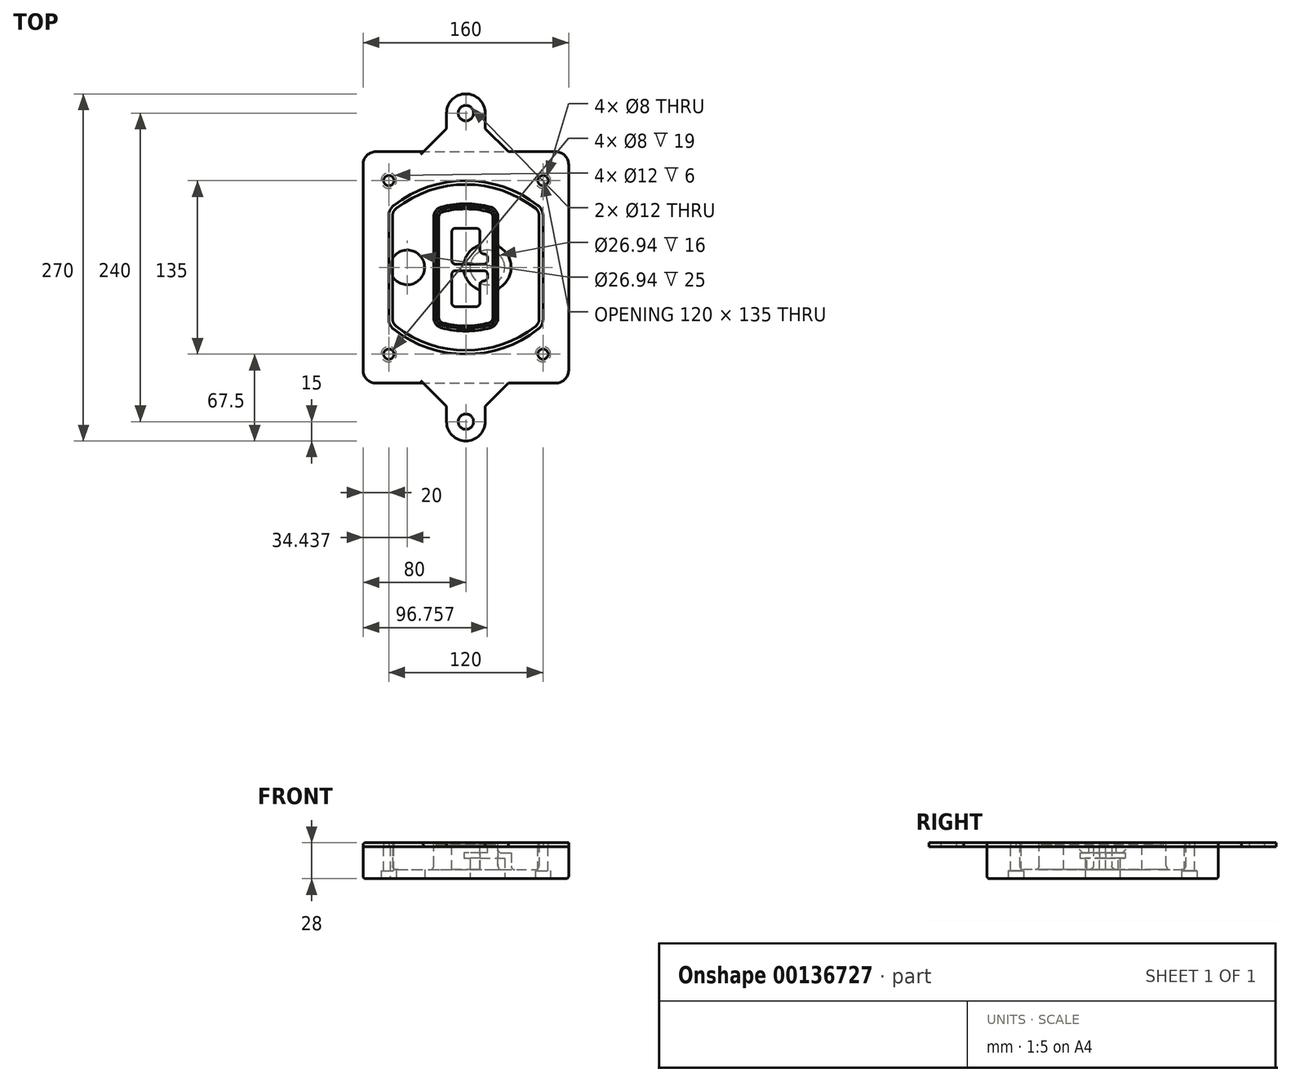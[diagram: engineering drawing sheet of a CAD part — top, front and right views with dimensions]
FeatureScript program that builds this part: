
annotation { "Feature Type Name" : "Feature", "Feature Type Description" : "" }
export const myFeature = defineFeature(function(context is Context, id is Id, definition is map)
    precondition{}
    {
        {
            var Q0;
            Q0=qCreatedBy(makeId("Top.planeOp"),FACE);
            var sketch = newSketch(context, id + "F0", { "sketchPlane" : qUnion([Q0])});
            skPoint(sketch, "E0.rect.middle", {"position": v(0, 0) * mm});
            skLineSegment(sketch, "E1.bottom", {"start": v(-70, -90) * mm, "end": v(70, -90) * mm});
            skLineSegment(sketch, "E1.top", {"start": v(-70, 90) * mm, "end": v(70, 90) * mm});
            skLineSegment(sketch, "E1.left", {"start": v(-80, -80) * mm, "end": v(-80, 80) * mm});
            skLineSegment(sketch, "E1.right", {"start": v(80, -80) * mm, "end": v(80, 80) * mm});
            skLineSegment(sketch, "E2", {"start": v(-80, 90) * mm, "end": v(80, -90) * mm, "construction": true});
            skLineSegment(sketch, "E3", {"start": v(80, 90) * mm, "end": v(-80, -90) * mm, "construction": true});
            skCircle(sketch, "E4", {"center": v(-60, 67.5) * mm, "radius": 4 * mm});
            skCircle(sketch, "E5", {"center": v(60, 67.5) * mm, "radius": 4 * mm});
            skCircle(sketch, "E6", {"center": v(60, -67.5) * mm, "radius": 4 * mm});
            skCircle(sketch, "E7", {"center": v(-60, -67.5) * mm, "radius": 4 * mm});
            skLineSegment(sketch, "E8", {"start": v(-60, 67.5) * mm, "end": v(60, 67.5) * mm, "construction": true});
            skLineSegment(sketch, "E9", {"start": v(60, 67.5) * mm, "end": v(60, -67.5) * mm, "construction": true});
            skLineSegment(sketch, "E10", {"start": v(60, -67.5) * mm, "end": v(-60, -67.5) * mm, "construction": true});
            skLineSegment(sketch, "E11", {"start": v(-60, -67.5) * mm, "end": v(-60, 67.5) * mm, "construction": true});
            skLineSegment(sketch, "E12", {"start": v(-60, 40.3) * mm, "end": v(-60, -40.3) * mm});
            skLineSegment(sketch, "E13", {"start": v(60, 40.3) * mm, "end": v(60, -40.3) * mm});
            skArc(sketch, "E14", {"start": v(56.15, 48.18) * mm, "mid": v(0, 67.5) * mm, "end": v(-56.15, 48.18) * mm});
            skArc(sketch, "E15", {"start": v(-56.15, -48.18) * mm, "mid": v(0, -67.5) * mm, "end": v(56.15, -48.18) * mm});
            skLineSegment(sketch, "E16", {"start": v(-60, 0) * mm, "end": v(60, 0) * mm, "construction": true});
            skPoint(sketch, "E17.visualSharp", {"position": v(-60, -45) * mm});
            skArc(sketch, "E17.filletArc", {"start": v(-60, -40.3) * mm, "mid": v(-58.99, -44.68) * mm, "end": v(-56.15, -48.18) * mm});
            skPoint(sketch, "E18.visualSharp", {"position": v(-60, 45) * mm});
            skArc(sketch, "E18.filletArc", {"start": v(-56.15, 48.18) * mm, "mid": v(-58.99, 44.68) * mm, "end": v(-60, 40.3) * mm});
            skPoint(sketch, "E19.visualSharp", {"position": v(60, 45) * mm});
            skArc(sketch, "E19.filletArc", {"start": v(60, 40.3) * mm, "mid": v(58.99, 44.68) * mm, "end": v(56.15, 48.18) * mm});
            skPoint(sketch, "E20.visualSharp", {"position": v(60, -45) * mm});
            skArc(sketch, "E20.filletArc", {"start": v(56.15, -48.18) * mm, "mid": v(58.99, -44.68) * mm, "end": v(60, -40.3) * mm});
            skPoint(sketch, "E21.visualSharp", {"position": v(-80, 90) * mm});
            skArc(sketch, "E21.filletArc", {"start": v(-70, 90) * mm, "mid": v(-77.07, 87.07) * mm, "end": v(-80, 80) * mm});
            skPoint(sketch, "E22.visualSharp", {"position": v(80, 90) * mm});
            skArc(sketch, "E22.filletArc", {"start": v(80, 80) * mm, "mid": v(77.07, 87.07) * mm, "end": v(70, 90) * mm});
            skPoint(sketch, "E23.visualSharp", {"position": v(80, -90) * mm});
            skArc(sketch, "E23.filletArc", {"start": v(70, -90) * mm, "mid": v(77.07, -87.07) * mm, "end": v(80, -80) * mm});
            skPoint(sketch, "E24.visualSharp", {"position": v(-80, -90) * mm});
            skArc(sketch, "E24.filletArc", {"start": v(-80, -80) * mm, "mid": v(-77.07, -87.07) * mm, "end": v(-70, -90) * mm});
            skArc(sketch, "E25.0", {"start": v(57, 40.3) * mm, "mid": v(56.3, 43.36) * mm, "end": v(54.3, 45.81) * mm});
            skLineSegment(sketch, "E25.1", {"start": v(57, 40.3) * mm, "end": v(57, -40.3) * mm});
            skArc(sketch, "E25.2", {"start": v(54.3, -45.81) * mm, "mid": v(56.3, -43.36) * mm, "end": v(57, -40.3) * mm});
            skArc(sketch, "E25.3", {"start": v(-54.3, -45.81) * mm, "mid": v(0, -64.5) * mm, "end": v(54.3, -45.81) * mm});
            skArc(sketch, "E25.4", {"start": v(-57, -40.3) * mm, "mid": v(-56.3, -43.36) * mm, "end": v(-54.3, -45.81) * mm});
            skArc(sketch, "E25.5", {"start": v(54.3, 45.81) * mm, "mid": v(0, 64.5) * mm, "end": v(-54.3, 45.81) * mm});
            skLineSegment(sketch, "E25.6", {"start": v(-57, 40.3) * mm, "end": v(-57, -40.3) * mm});
            skArc(sketch, "E25.7", {"start": v(-54.3, 45.81) * mm, "mid": v(-56.3, 43.36) * mm, "end": v(-57, 40.3) * mm});
            skArc(sketch, "E26.0", {"start": v(-58.62, 51.33) * mm, "mid": v(-62.58, 46.43) * mm, "end": v(-64, 40.3) * mm});
            skArc(sketch, "E26.1", {"start": v(58.62, 51.33) * mm, "mid": v(0, 71.5) * mm, "end": v(-58.62, 51.33) * mm});
            skArc(sketch, "E26.2", {"start": v(64, 40.3) * mm, "mid": v(62.58, 46.43) * mm, "end": v(58.62, 51.33) * mm});
            skLineSegment(sketch, "E26.3", {"start": v(64, 40.3) * mm, "end": v(64, -40.3) * mm});
            skArc(sketch, "E26.4", {"start": v(58.62, -51.33) * mm, "mid": v(62.58, -46.43) * mm, "end": v(64, -40.3) * mm});
            skLineSegment(sketch, "E26.5", {"start": v(-64, 40.3) * mm, "end": v(-64, -40.3) * mm});
            skArc(sketch, "E26.6", {"start": v(-58.62, -51.33) * mm, "mid": v(0, -71.5) * mm, "end": v(58.62, -51.33) * mm});
            skArc(sketch, "E26.7", {"start": v(-64, -40.3) * mm, "mid": v(-62.58, -46.43) * mm, "end": v(-58.62, -51.33) * mm});
            skSolve(sketch);
        }
        {
            var Q0;
            Q0=makeQuery(id+"F0.imprint","IMPRINT",FACE,{"disambiguationData":[TD([[makeQuery(id+"F0.imprint","IMPRINT",EDGE,{"derivedFrom":sQuery(id+"F0.wireOp",EDGE,"E1.bottom")}),1.0]])]});
            var Q1;
            Q1=makeQuery(id+"F0.imprint","IMPRINT",FACE,{"disambiguationData":[TD([[makeQuery(id+"F0.imprint","IMPRINT",EDGE,{"derivedFrom":sQuery(id+"F0.wireOp",EDGE,"E12")}),1.0]])]});
            var Q2;
            Q2=makeQuery(id+"F0.imprint","IMPRINT",FACE,{"disambiguationData":[TD([[makeQuery(id+"F0.imprint","IMPRINT",EDGE,{"derivedFrom":sQuery(id+"F0.wireOp",EDGE,"E25.0")}),1.0]])]});
            var Q3;
            Q3=makeQuery(id+"F0.imprint","IMPRINT",FACE,{"disambiguationData":[TD([[makeQuery(id+"F0.imprint","IMPRINT",EDGE,{"derivedFrom":sQuery(id+"F0.wireOp",EDGE,"E12")}),-1.0]])]});
            extrude(context, id + "F1", {"entities" : qUnion([Q0, Q1, Q2, Q3]), "oppositeDirection" : true, "depth" : 25 * mm});
        }
        {
            var Q0;
            Q0=makeQuery(id+"F0.imprint","IMPRINT",FACE,{"disambiguationData":[TD([[makeQuery(id+"F0.imprint","IMPRINT",EDGE,{"derivedFrom":sQuery(id+"F0.wireOp",EDGE,"E12")}),1.0]])]});
            extrude(context, id + "F2", {"entities" : qUnion([Q0]), "operationType" : NewBodyOperationType.ADD, "depth" : 3 * mm});
        }
        {
            var Q0;
            Q0=makeQuery(id+"F0.imprint","IMPRINT",FACE,{"disambiguationData":[TD([[makeQuery(id+"F0.imprint","IMPRINT",EDGE,{"derivedFrom":sQuery(id+"F0.wireOp",EDGE,"E25.0")}),1.0]])]});
            extrude(context, id + "F3", {"entities" : qUnion([Q0]), "operationType" : NewBodyOperationType.REMOVE, "oppositeDirection" : true, "depth" : 18 * mm});
        }
        {
            var Q0;
            Q0=makeQuery(id+"F2.opExtrude","CAP_FACE",FACE,{"disambiguationData":[OSD([sQuery(id+"F0.wireOp",EDGE,"E12"),sQuery(id+"F0.wireOp",EDGE,"E13"),sQuery(id+"F0.wireOp",EDGE,"E14"),sQuery(id+"F0.wireOp",EDGE,"E15"),sQuery(id+"F0.wireOp",EDGE,"E17.filletArc"),sQuery(id+"F0.wireOp",EDGE,"E18.filletArc"),sQuery(id+"F0.wireOp",EDGE,"E19.filletArc"),sQuery(id+"F0.wireOp",EDGE,"E20.filletArc"),sQuery(id+"F0.wireOp",EDGE,"E25.0"),sQuery(id+"F0.wireOp",EDGE,"E25.1"),sQuery(id+"F0.wireOp",EDGE,"E25.2"),sQuery(id+"F0.wireOp",EDGE,"E25.3"),sQuery(id+"F0.wireOp",EDGE,"E25.4"),sQuery(id+"F0.wireOp",EDGE,"E25.5"),sQuery(id+"F0.wireOp",EDGE,"E25.6"),sQuery(id+"F0.wireOp",EDGE,"E25.7")])],"isStart":false});
            var sketch = newSketch(context, id + "F4", { "sketchPlane" : qUnion([Q0])});
            skArc(sketch, "E27.0", {"start": v(-19.08, -46.97) * mm, "mid": v(0, -49.5) * mm, "end": v(19.08, -46.97) * mm});
            skArc(sketch, "E28.0", {"start": v(19.08, 46.97) * mm, "mid": v(0, 49.5) * mm, "end": v(-19.08, 46.97) * mm});
            skLineSegment(sketch, "E29", {"start": v(-25, 39.25) * mm, "end": v(-25, -39.25) * mm});
            skLineSegment(sketch, "E30", {"start": v(25, 39.25) * mm, "end": v(25, -39.25) * mm});
            skLineSegment(sketch, "E31", {"start": v(-25, 45.1) * mm, "end": v(25, 45.1) * mm, "construction": true});
            skLineSegment(sketch, "E32", {"start": v(-25, -45.1) * mm, "end": v(25, -45.1) * mm, "construction": true});
            skPoint(sketch, "E33.visualSharp", {"position": v(-25, 45.1) * mm});
            skArc(sketch, "E33.filletArc", {"start": v(-19.08, 46.97) * mm, "mid": v(-23.35, 44.11) * mm, "end": v(-25, 39.25) * mm});
            skPoint(sketch, "E34.visualSharp", {"position": v(25, 45.1) * mm});
            skArc(sketch, "E34.filletArc", {"start": v(25, 39.25) * mm, "mid": v(23.35, 44.11) * mm, "end": v(19.08, 46.97) * mm});
            skPoint(sketch, "E35.visualSharp", {"position": v(25, -45.1) * mm});
            skArc(sketch, "E35.filletArc", {"start": v(19.08, -46.97) * mm, "mid": v(23.35, -44.11) * mm, "end": v(25, -39.25) * mm});
            skPoint(sketch, "E36.visualSharp", {"position": v(-25, -45.1) * mm});
            skArc(sketch, "E36.filletArc", {"start": v(-25, -39.25) * mm, "mid": v(-23.35, -44.11) * mm, "end": v(-19.08, -46.97) * mm});
            skArc(sketch, "E37.0", {"start": v(54.3, 45.81) * mm, "mid": v(0, 64.5) * mm, "end": v(-54.3, 45.81) * mm});
            skArc(sketch, "E37.1", {"start": v(-54.3, 45.81) * mm, "mid": v(-56.3, 43.36) * mm, "end": v(-57, 40.3) * mm});
            skLineSegment(sketch, "E37.2", {"start": v(-57, 40.3) * mm, "end": v(-57, -40.3) * mm});
            skArc(sketch, "E37.3", {"start": v(-57, -40.3) * mm, "mid": v(-56.3, -43.36) * mm, "end": v(-54.3, -45.81) * mm});
            skArc(sketch, "E37.4", {"start": v(-54.3, -45.81) * mm, "mid": v(0, -64.5) * mm, "end": v(54.3, -45.81) * mm});
            skArc(sketch, "E37.5", {"start": v(54.3, -45.81) * mm, "mid": v(56.3, -43.36) * mm, "end": v(57, -40.3) * mm});
            skLineSegment(sketch, "E37.6", {"start": v(57, 40.3) * mm, "end": v(57, -40.3) * mm});
            skArc(sketch, "E37.7", {"start": v(57, 40.3) * mm, "mid": v(56.3, 43.36) * mm, "end": v(54.3, 45.81) * mm});
            skLineSegment(sketch, "E38.0", {"start": v(23, 39.25) * mm, "end": v(23, -39.25) * mm});
            skArc(sketch, "E38.1", {"start": v(18.56, -45.04) * mm, "mid": v(21.76, -42.9) * mm, "end": v(23, -39.25) * mm});
            skArc(sketch, "E38.2", {"start": v(-18.56, -45.04) * mm, "mid": v(0, -47.5) * mm, "end": v(18.56, -45.04) * mm});
            skArc(sketch, "E38.3", {"start": v(-23, -39.25) * mm, "mid": v(-21.76, -42.9) * mm, "end": v(-18.56, -45.04) * mm});
            skLineSegment(sketch, "E38.4", {"start": v(-23, 39.25) * mm, "end": v(-23, -39.25) * mm});
            skArc(sketch, "E38.5", {"start": v(23, 39.25) * mm, "mid": v(21.76, 42.9) * mm, "end": v(18.56, 45.04) * mm});
            skArc(sketch, "E38.6", {"start": v(-18.56, 45.04) * mm, "mid": v(-21.76, 42.9) * mm, "end": v(-23, 39.25) * mm});
            skArc(sketch, "E38.7", {"start": v(18.56, 45.04) * mm, "mid": v(0, 47.5) * mm, "end": v(-18.56, 45.04) * mm});
            skArc(sketch, "E39.0", {"start": v(21, 39.25) * mm, "mid": v(20.18, 41.68) * mm, "end": v(18.04, 43.1) * mm});
            skLineSegment(sketch, "E39.1", {"start": v(21, 39.25) * mm, "end": v(21, -39.25) * mm});
            skArc(sketch, "E39.2", {"start": v(18.04, -43.1) * mm, "mid": v(20.18, -41.68) * mm, "end": v(21, -39.25) * mm});
            skArc(sketch, "E39.3", {"start": v(-18.04, -43.1) * mm, "mid": v(0, -45.5) * mm, "end": v(18.04, -43.1) * mm});
            skArc(sketch, "E39.4", {"start": v(-21, -39.25) * mm, "mid": v(-20.18, -41.68) * mm, "end": v(-18.04, -43.1) * mm});
            skArc(sketch, "E39.5", {"start": v(18.04, 43.1) * mm, "mid": v(0, 45.5) * mm, "end": v(-18.04, 43.1) * mm});
            skLineSegment(sketch, "E39.6", {"start": v(-21, 39.25) * mm, "end": v(-21, -39.25) * mm});
            skArc(sketch, "E39.7", {"start": v(-18.04, 43.1) * mm, "mid": v(-20.18, 41.68) * mm, "end": v(-21, 39.25) * mm});
            skLineSegment(sketch, "E40", {"start": v(-25, 0) * mm, "end": v(25, 0) * mm, "construction": true});
            skLineSegment(sketch, "E41", {"start": v(-11, 5.5) * mm, "end": v(-11, 27.5) * mm});
            skLineSegment(sketch, "E42", {"start": v(-8, 30.5) * mm, "end": v(8, 30.5) * mm});
            skLineSegment(sketch, "E43", {"start": v(11, 27.5) * mm, "end": v(11, 13.5) * mm});
            skLineSegment(sketch, "E44", {"start": v(14, 10.5) * mm, "end": v(14, 10.5) * mm});
            skLineSegment(sketch, "E45", {"start": v(17, 7.5) * mm, "end": v(17, 5.5) * mm});
            skLineSegment(sketch, "E46", {"start": v(14, 2.5) * mm, "end": v(-8, 2.5) * mm});
            skPoint(sketch, "E47.visualSharp", {"position": v(-11, 30.5) * mm});
            skArc(sketch, "E47.filletArc", {"start": v(-8, 30.5) * mm, "mid": v(-10.12, 29.62) * mm, "end": v(-11, 27.5) * mm});
            skPoint(sketch, "E48.visualSharp", {"position": v(11, 30.5) * mm});
            skArc(sketch, "E48.filletArc", {"start": v(11, 27.5) * mm, "mid": v(10.12, 29.62) * mm, "end": v(8, 30.5) * mm});
            skPoint(sketch, "E49.visualSharp", {"position": v(11, 10.5) * mm});
            skArc(sketch, "E49.filletArc", {"start": v(11, 13.5) * mm, "mid": v(11.88, 11.38) * mm, "end": v(14, 10.5) * mm});
            skPoint(sketch, "E50.visualSharp", {"position": v(17, 10.5) * mm});
            skArc(sketch, "E50.filletArc", {"start": v(17, 7.5) * mm, "mid": v(16.12, 9.62) * mm, "end": v(14, 10.5) * mm});
            skPoint(sketch, "E51.visualSharp", {"position": v(17, 2.5) * mm});
            skArc(sketch, "E51.filletArc", {"start": v(14, 2.5) * mm, "mid": v(16.12, 3.38) * mm, "end": v(17, 5.5) * mm});
            skPoint(sketch, "E52.visualSharp", {"position": v(-11, 2.5) * mm});
            skArc(sketch, "E52.filletArc", {"start": v(-11, 5.5) * mm, "mid": v(-10.12, 3.38) * mm, "end": v(-8, 2.5) * mm});
            skLineSegment(sketch, "E53.0.MirrorCS", {"start": v(14, -2.5) * mm, "end": v(-8, -2.5) * mm});
            skArc(sketch, "E54.0.MirrorCS", {"start": v(-11, -5.5) * mm, "mid": v(-10.12, -3.38) * mm, "end": v(-8, -2.5) * mm});
            skLineSegment(sketch, "E55.0.MirrorCS", {"start": v(-11, -5.5) * mm, "end": v(-11, -27.5) * mm});
            skArc(sketch, "E56.0.MirrorCS", {"start": v(-8, -30.5) * mm, "mid": v(-10.12, -29.62) * mm, "end": v(-11, -27.5) * mm});
            skLineSegment(sketch, "E57.0.MirrorCS", {"start": v(-8, -30.5) * mm, "end": v(8, -30.5) * mm});
            skArc(sketch, "E58.0.MirrorCS", {"start": v(11, -27.5) * mm, "mid": v(10.12, -29.62) * mm, "end": v(8, -30.5) * mm});
            skLineSegment(sketch, "E59.0.MirrorCS", {"start": v(11, -27.5) * mm, "end": v(11, -13.5) * mm});
            skArc(sketch, "E60.0.MirrorCS", {"start": v(11, -13.5) * mm, "mid": v(11.88, -11.38) * mm, "end": v(14, -10.5) * mm});
            skArc(sketch, "E61.0.MirrorCS", {"start": v(17, -7.5) * mm, "mid": v(16.12, -9.62) * mm, "end": v(14, -10.5) * mm});
            skLineSegment(sketch, "E62.0.MirrorCS", {"start": v(17, -7.5) * mm, "end": v(17, -5.5) * mm});
            skArc(sketch, "E63.0.MirrorCS", {"start": v(14, -2.5) * mm, "mid": v(16.12, -3.38) * mm, "end": v(17, -5.5) * mm});
            skSolve(sketch);
        }
        {
            var Q0;
            Q0=makeQuery(id+"F4.imprint","IMPRINT",FACE,{"disambiguationData":[TD([[makeQuery(id+"F4.imprint","IMPRINT",EDGE,{"derivedFrom":sQuery(id+"F4.wireOp",EDGE,"E27.0")}),1.0]])]});
            var Q1;
            Q1=makeQuery(id+"F4.imprint","IMPRINT",FACE,{"disambiguationData":[TD([[makeQuery(id+"F4.imprint","IMPRINT",EDGE,{"derivedFrom":sQuery(id+"F4.wireOp",EDGE,"E38.0")}),-1.0]])]});
            var Q2;
            Q2=makeQuery(id+"F4.imprint","IMPRINT",FACE,{"disambiguationData":[TD([[makeQuery(id+"F4.imprint","IMPRINT",EDGE,{"derivedFrom":sQuery(id+"F4.wireOp",EDGE,"E39.0")}),1.0]])]});
            extrude(context, id + "F5", {"entities" : qUnion([Q0, Q1, Q2]), "operationType" : NewBodyOperationType.ADD, "endBound" : BoundingType.UP_TO_NEXT, "oppositeDirection" : true, "depth" : 25 * mm});
        }
        {
            var Q0;
            Q0=makeQuery(id+"F4.imprint","IMPRINT",FACE,{"disambiguationData":[TD([[makeQuery(id+"F4.imprint","IMPRINT",EDGE,{"derivedFrom":sQuery(id+"F4.wireOp",EDGE,"E38.0")}),-1.0]])]});
            extrude(context, id + "F6", {"entities" : qUnion([Q0]), "operationType" : NewBodyOperationType.REMOVE, "oppositeDirection" : true, "depth" : 2 * mm});
        }
        {
            var Q0;
            Q0=makeQuery(id+"F1.opExtrude","CAP_FACE",FACE,{"disambiguationData":[OSD([sQuery(id+"F0.wireOp",EDGE,"E1.bottom"),sQuery(id+"F0.wireOp",EDGE,"E1.top"),sQuery(id+"F0.wireOp",EDGE,"E1.left"),sQuery(id+"F0.wireOp",EDGE,"E1.right"),sQuery(id+"F0.wireOp",EDGE,"E4"),sQuery(id+"F0.wireOp",EDGE,"E5"),sQuery(id+"F0.wireOp",EDGE,"E6"),sQuery(id+"F0.wireOp",EDGE,"E7"),sQuery(id+"F0.wireOp",EDGE,"E21.filletArc"),sQuery(id+"F0.wireOp",EDGE,"E22.filletArc"),sQuery(id+"F0.wireOp",EDGE,"E23.filletArc"),sQuery(id+"F0.wireOp",EDGE,"E24.filletArc")])],"isStart":false});
            var sketch = newSketch(context, id + "F7", { "sketchPlane" : qUnion([Q0])});
            skCircle(sketch, "E64", {"center": v(16.76, 0) * mm, "radius": 13.47 * mm});
            skCircle(sketch, "E65", {"center": v(-45.56, 0) * mm, "radius": 13.47 * mm});
            skLineSegment(sketch, "E66", {"start": v(80, 0) * mm, "end": v(-80, 0) * mm});
            skCircle(sketch, "E67", {"center": v(16.76, 0) * mm, "radius": 18.47 * mm});
            skCircle(sketch, "E68", {"center": v(60, -67.5) * mm, "radius": 6 * mm});
            skCircle(sketch, "E69", {"center": v(-60, -67.5) * mm, "radius": 6 * mm});
            skCircle(sketch, "E70", {"center": v(-60, 67.5) * mm, "radius": 6 * mm});
            skCircle(sketch, "E71", {"center": v(60, 67.5) * mm, "radius": 6 * mm});
            skSolve(sketch);
        }
        {
            var Q0;
            {var subQ1=sQuery(id+"F7.wireOp",EDGE,"E66");var subQ4=sQuery(id+"F7.wireOp",EDGE,"E64");var subQ6=makeQuery(id+"F7.imprint","INTERSECT",VERTEX,{"disambiguationData":[OD(0.0)],"derivedFrom":[subQ4,subQ1]});Q0=makeQuery(id+"F7.imprint","IMPRINT",FACE,{"disambiguationData":[TD([[makeQuery(id+"F7.imprint","IMPRINT",EDGE,{"disambiguationData":[TD([[subQ6,-1.0]])],"derivedFrom":subQ4}),-1.0]])]});}
            var Q1;
            {var subQ0=sQuery(id+"F7.wireOp",EDGE,"E66");var subQ1=sQuery(id+"F7.wireOp",EDGE,"E64");var subQ3=makeQuery(id+"F7.imprint","INTERSECT",VERTEX,{"disambiguationData":[OD(0.0)],"derivedFrom":[subQ1,subQ0]});Q1=makeQuery(id+"F7.imprint","IMPRINT",FACE,{"disambiguationData":[TD([[makeQuery(id+"F7.imprint","IMPRINT",EDGE,{"disambiguationData":[TD([[subQ3,-1.0]])],"derivedFrom":subQ1}),1.0]])]});}
            var Q2;
            {var subQ0=sQuery(id+"F7.wireOp",EDGE,"E66");var subQ1=sQuery(id+"F7.wireOp",EDGE,"E64");var subQ3=makeQuery(id+"F7.imprint","INTERSECT",VERTEX,{"disambiguationData":[OD(0.0)],"derivedFrom":[subQ1,subQ0]});Q2=makeQuery(id+"F7.imprint","IMPRINT",FACE,{"disambiguationData":[TD([[makeQuery(id+"F7.imprint","IMPRINT",EDGE,{"disambiguationData":[TD([[subQ3,1.0]])],"derivedFrom":subQ1}),1.0]])]});}
            var Q3;
            {var subQ1=sQuery(id+"F7.wireOp",EDGE,"E66");var subQ4=sQuery(id+"F7.wireOp",EDGE,"E64");var subQ6=makeQuery(id+"F7.imprint","INTERSECT",VERTEX,{"disambiguationData":[OD(0.0)],"derivedFrom":[subQ4,subQ1]});Q3=makeQuery(id+"F7.imprint","IMPRINT",FACE,{"disambiguationData":[TD([[makeQuery(id+"F7.imprint","IMPRINT",EDGE,{"disambiguationData":[TD([[subQ6,1.0]])],"derivedFrom":subQ4}),-1.0]])]});}
            extrude(context, id + "F8", {"entities" : qUnion([Q0, Q1, Q2, Q3]), "operationType" : NewBodyOperationType.ADD, "oppositeDirection" : true, "depth" : 20 * mm});
        }
        {
            var Q0;
            {var subQ0=sQuery(id+"F7.wireOp",EDGE,"E66");var subQ1=sQuery(id+"F7.wireOp",EDGE,"E64");var subQ3=makeQuery(id+"F7.imprint","INTERSECT",VERTEX,{"disambiguationData":[OD(0.0)],"derivedFrom":[subQ1,subQ0]});Q0=makeQuery(id+"F7.imprint","IMPRINT",FACE,{"disambiguationData":[TD([[makeQuery(id+"F7.imprint","IMPRINT",EDGE,{"disambiguationData":[TD([[subQ3,-1.0]])],"derivedFrom":subQ1}),1.0]])]});}
            var Q1;
            {var subQ0=sQuery(id+"F7.wireOp",EDGE,"E66");var subQ1=sQuery(id+"F7.wireOp",EDGE,"E64");var subQ3=makeQuery(id+"F7.imprint","INTERSECT",VERTEX,{"disambiguationData":[OD(0.0)],"derivedFrom":[subQ1,subQ0]});Q1=makeQuery(id+"F7.imprint","IMPRINT",FACE,{"disambiguationData":[TD([[makeQuery(id+"F7.imprint","IMPRINT",EDGE,{"disambiguationData":[TD([[subQ3,1.0]])],"derivedFrom":subQ1}),1.0]])]});}
            extrude(context, id + "F9", {"entities" : qUnion([Q0, Q1]), "operationType" : NewBodyOperationType.REMOVE, "oppositeDirection" : true, "depth" : 16 * mm});
        }
        {
            var Q0;
            {var subQ0=sQuery(id+"F7.wireOp",EDGE,"E66");var subQ1=sQuery(id+"F7.wireOp",EDGE,"E65");var subQ3=makeQuery(id+"F7.imprint","INTERSECT",VERTEX,{"disambiguationData":[OD(0.0)],"derivedFrom":[subQ1,subQ0]});Q0=makeQuery(id+"F7.imprint","IMPRINT",FACE,{"disambiguationData":[TD([[makeQuery(id+"F7.imprint","IMPRINT",EDGE,{"disambiguationData":[TD([[subQ3,-1.0]])],"derivedFrom":subQ1}),1.0]])]});}
            var Q1;
            {var subQ0=sQuery(id+"F7.wireOp",EDGE,"E66");var subQ1=sQuery(id+"F7.wireOp",EDGE,"E65");var subQ3=makeQuery(id+"F7.imprint","INTERSECT",VERTEX,{"disambiguationData":[OD(0.0)],"derivedFrom":[subQ1,subQ0]});Q1=makeQuery(id+"F7.imprint","IMPRINT",FACE,{"disambiguationData":[TD([[makeQuery(id+"F7.imprint","IMPRINT",EDGE,{"disambiguationData":[TD([[subQ3,1.0]])],"derivedFrom":subQ1}),1.0]])]});}
            extrude(context, id + "F10", {"entities" : qUnion([Q0, Q1]), "operationType" : NewBodyOperationType.REMOVE, "oppositeDirection" : true, "depth" : 25 * mm});
        }
        {
            var Q0;
            Q0=makeQuery(id+"F7.imprint","IMPRINT",FACE,{"disambiguationData":[TD([[makeQuery(id+"F7.imprint","IMPRINT",EDGE,{"derivedFrom":sQuery(id+"F7.wireOp",EDGE,"E68")}),1.0]])]});
            var Q1;
            Q1=makeQuery(id+"F7.imprint","IMPRINT",FACE,{"disambiguationData":[TD([[makeQuery(id+"F7.imprint","IMPRINT",EDGE,{"derivedFrom":makeQuery(id+"F1.opExtrude","CAP_EDGE",EDGE,{"disambiguationData":[OSD([sQuery(id+"F0.wireOp",EDGE,"E5")])],"isStart":false})}),-1.0]])]});
            var Q2;
            Q2=makeQuery(id+"F7.imprint","IMPRINT",FACE,{"disambiguationData":[TD([[makeQuery(id+"F7.imprint","IMPRINT",EDGE,{"derivedFrom":sQuery(id+"F7.wireOp",EDGE,"E69")}),1.0]])]});
            var Q3;
            Q3=makeQuery(id+"F7.imprint","IMPRINT",FACE,{"disambiguationData":[TD([[makeQuery(id+"F7.imprint","IMPRINT",EDGE,{"derivedFrom":makeQuery(id+"F1.opExtrude","CAP_EDGE",EDGE,{"disambiguationData":[OSD([sQuery(id+"F0.wireOp",EDGE,"E4")])],"isStart":false})}),-1.0]])]});
            var Q4;
            Q4=makeQuery(id+"F7.imprint","IMPRINT",FACE,{"disambiguationData":[TD([[makeQuery(id+"F7.imprint","IMPRINT",EDGE,{"derivedFrom":sQuery(id+"F7.wireOp",EDGE,"E70")}),1.0]])]});
            var Q5;
            Q5=makeQuery(id+"F7.imprint","IMPRINT",FACE,{"disambiguationData":[TD([[makeQuery(id+"F7.imprint","IMPRINT",EDGE,{"derivedFrom":makeQuery(id+"F1.opExtrude","CAP_EDGE",EDGE,{"disambiguationData":[OSD([sQuery(id+"F0.wireOp",EDGE,"E7")])],"isStart":false})}),-1.0]])]});
            var Q6;
            Q6=makeQuery(id+"F7.imprint","IMPRINT",FACE,{"disambiguationData":[TD([[makeQuery(id+"F7.imprint","IMPRINT",EDGE,{"derivedFrom":sQuery(id+"F7.wireOp",EDGE,"E71")}),1.0]])]});
            var Q7;
            Q7=makeQuery(id+"F7.imprint","IMPRINT",FACE,{"disambiguationData":[TD([[makeQuery(id+"F7.imprint","IMPRINT",EDGE,{"derivedFrom":makeQuery(id+"F1.opExtrude","CAP_EDGE",EDGE,{"disambiguationData":[OSD([sQuery(id+"F0.wireOp",EDGE,"E6")])],"isStart":false})}),-1.0]])]});
            extrude(context, id + "F11", {"entities" : qUnion([Q0, Q1, Q2, Q3, Q4, Q5, Q6, Q7]), "operationType" : NewBodyOperationType.REMOVE, "oppositeDirection" : true, "depth" : 6 * mm});
        }
        {
            var Q0;
            Q0=makeQuery(id+"F9.boolean.opBoolean","COPY",FACE,{"derivedFrom":makeQuery(id+"F9.opExtrude","CAP_FACE",FACE,{"disambiguationData":[OSD([sQuery(id+"F7.wireOp",EDGE,"E64")])],"isStart":false})});
            var sketch = newSketch(context, id + "F12", { "sketchPlane" : qUnion([Q0])});
            skArc(sketch, "E72.0", {"start": v(11, 17.55) * mm, "mid": v(2.57, 11.82) * mm, "end": v(-1.54, 2.5) * mm});
            skArc(sketch, "E72.1", {"start": v(-1.54, -2.5) * mm, "mid": v(2.57, -11.82) * mm, "end": v(11, -17.55) * mm});
            skLineSegment(sketch, "E73", {"start": v(-1.54, -2.5) * mm, "end": v(14, -2.5) * mm});
            skLineSegment(sketch, "E74.0", {"start": v(14, 2.5) * mm, "end": v(-1.54, 2.5) * mm});
            skArc(sketch, "E74.1", {"start": v(14, 2.5) * mm, "mid": v(16.12, 3.38) * mm, "end": v(17, 5.5) * mm});
            skLineSegment(sketch, "E74.2", {"start": v(17, 7.5) * mm, "end": v(17, 5.5) * mm});
            skArc(sketch, "E74.3", {"start": v(17, 7.5) * mm, "mid": v(16.12, 9.62) * mm, "end": v(14, 10.5) * mm});
            skArc(sketch, "E74.4", {"start": v(11, 13.5) * mm, "mid": v(11.88, 11.38) * mm, "end": v(14, 10.5) * mm});
            skLineSegment(sketch, "E74.5", {"start": v(11, 17.55) * mm, "end": v(11, 13.5) * mm});
            skLineSegment(sketch, "E74.7", {"start": v(14, -2.5) * mm, "end": v(-1.54, -2.5) * mm});
            skArc(sketch, "E74.8", {"start": v(14, -2.5) * mm, "mid": v(16.12, -3.38) * mm, "end": v(17, -5.5) * mm});
            skLineSegment(sketch, "E74.9", {"start": v(17, -7.5) * mm, "end": v(17, -5.5) * mm});
            skArc(sketch, "E74.10", {"start": v(17, -7.5) * mm, "mid": v(16.12, -9.62) * mm, "end": v(14, -10.5) * mm});
            skArc(sketch, "E74.11", {"start": v(11, -13.5) * mm, "mid": v(11.88, -11.38) * mm, "end": v(14, -10.5) * mm});
            skLineSegment(sketch, "E74.12", {"start": v(11, -17.55) * mm, "end": v(11, -13.5) * mm});
            skPoint(sketch, "E75.orphan", {"position": v(11, -27.5) * mm});
            skPoint(sketch, "E76.orphan", {"position": v(-8, -2.5) * mm});
            skPoint(sketch, "E77.orphan", {"position": v(-8, 2.5) * mm});
            skPoint(sketch, "E78.orphan", {"position": v(11, 27.5) * mm});
            skSolve(sketch);
        }
        {
            var Q0;
            {var subQ7=sQuery(id+"F12.wireOp",EDGE,"E72.0");var subQ14=sQuery(id+"F12.wireOp",EDGE,"E72.1");var subQ16=sQuery(id+"F12.wireOp",EDGE,"E74.1");var subQ18=sQuery(id+"F12.wireOp",EDGE,"E74.8");Q0=qUnion([makeQuery(id+"F12.imprint","IMPRINT",FACE,{"disambiguationData":[TD([[makeQuery(id+"F12.imprint","IMPRINT",EDGE,{"derivedFrom":subQ7}),1.0]])]}),makeQuery(id+"F12.imprint","IMPRINT",FACE,{"disambiguationData":[TD([[makeQuery(id+"F12.imprint","IMPRINT",EDGE,{"derivedFrom":subQ14}),1.0]])]}),makeQuery(id+"F12.imprint","IMPRINT",FACE,{"disambiguationData":[TD([[makeQuery(id+"F12.imprint","IMPRINT",EDGE,{"derivedFrom":subQ16}),1.0]])]}),makeQuery(id+"F12.imprint","IMPRINT",FACE,{"disambiguationData":[TD([[makeQuery(id+"F12.imprint","IMPRINT",EDGE,{"derivedFrom":subQ18}),-1.0]])]})]);}
            var Q1;
            Q1=makeQuery(id+"F5.boolean.opBoolean","SPLIT",FACE,{"disambiguationData":[TD([makeQuery(id+"F5.opExtrude","SWEPT_FACE",FACE,{"disambiguationData":[OSD([sQuery(id+"F4.wireOp",EDGE,"E41")])]})])],"derivedFrom":makeQuery(id+"F3.boolean.opBoolean","COPY",FACE,{"derivedFrom":makeQuery(id+"F3.opExtrude","CAP_FACE",FACE,{"disambiguationData":[OSD([sQuery(id+"F0.wireOp",EDGE,"E25.0"),sQuery(id+"F0.wireOp",EDGE,"E25.1"),sQuery(id+"F0.wireOp",EDGE,"E25.2"),sQuery(id+"F0.wireOp",EDGE,"E25.3"),sQuery(id+"F0.wireOp",EDGE,"E25.4"),sQuery(id+"F0.wireOp",EDGE,"E25.5"),sQuery(id+"F0.wireOp",EDGE,"E25.6"),sQuery(id+"F0.wireOp",EDGE,"E25.7")])],"isStart":false})})});
            extrude(context, id + "F13", {"entities" : qUnion([Q0]), "operationType" : NewBodyOperationType.REMOVE, "endBound" : BoundingType.UP_TO_SURFACE, "endBoundEntityFace" : qUnion([Q1]), "depth" : 25 * mm});
        }
        {
            var Q0;
            Q0=makeQuery(id+"F3.boolean.opBoolean","COPY",EDGE,{"derivedFrom":makeQuery(id+"F3.opExtrude","CAP_EDGE",EDGE,{"disambiguationData":[OSD([sQuery(id+"F0.wireOp",EDGE,"E25.6")])],"isStart":false})});
            var Q1;
            Q1=makeQuery(id+"F8.boolean.opBoolean","INTERSECT",EDGE,{"derivedFrom":[makeQuery(id+"F5.opExtrude","SWEPT_FACE",FACE,{"disambiguationData":[OSD([sQuery(id+"F4.wireOp",EDGE,"E30")])]}),makeQuery(id+"F8.opExtrude","CAP_FACE",FACE,{"disambiguationData":[OSD([sQuery(id+"F7.wireOp",EDGE,"E67")])],"isStart":false})]});
            var Q2;
            Q2=makeQuery(id+"F8.boolean.opBoolean","INTERSECT",EDGE,{"disambiguationData":[OD(1.0)],"derivedFrom":[makeQuery(id+"F5.opExtrude","SWEPT_FACE",FACE,{"disambiguationData":[OSD([sQuery(id+"F4.wireOp",EDGE,"E30")])]}),makeQuery(id+"F8.opExtrude","SWEPT_FACE",FACE,{"disambiguationData":[OSD([sQuery(id+"F7.wireOp",EDGE,"E67")])]})]});
            var Q3;
            {var subQ0=sQuery(id+"F4.wireOp",EDGE,"E30");Q3=makeQuery(id+"F8.boolean.opBoolean","SPLIT",EDGE,{"disambiguationData":[TD([makeQuery(id+"F5.opExtrude","SWEPT_FACE",FACE,{"disambiguationData":[OSD([sQuery(id+"F4.wireOp",EDGE,"E35.filletArc")])]})])],"derivedFrom":makeQuery(id+"F5.opExtrude","CAP_EDGE",EDGE,{"disambiguationData":[OSD([subQ0])],"isStart":false})});}
            var Q4;
            {var subQ0=sQuery(id+"F0.wireOp",EDGE,"E25.7");var subQ1=sQuery(id+"F0.wireOp",EDGE,"E25.1");var subQ2=sQuery(id+"F0.wireOp",EDGE,"E25.6");var subQ3=sQuery(id+"F0.wireOp",EDGE,"E25.5");var subQ4=sQuery(id+"F0.wireOp",EDGE,"E25.4");var subQ5=sQuery(id+"F0.wireOp",EDGE,"E25.0");var subQ6=sQuery(id+"F0.wireOp",EDGE,"E25.2");var subQ7=sQuery(id+"F0.wireOp",EDGE,"E25.3");Q4=makeQuery(id+"F8.boolean.opBoolean","INTERSECT",EDGE,{"derivedFrom":[makeQuery(id+"F5.boolean.opBoolean","SPLIT",FACE,{"disambiguationData":[TD([makeQuery(id+"F2.opExtrude","SWEPT_FACE",FACE,{"disambiguationData":[OSD([subQ5])]})])],"derivedFrom":makeQuery(id+"F3.boolean.opBoolean","COPY",FACE,{"derivedFrom":makeQuery(id+"F3.opExtrude","CAP_FACE",FACE,{"disambiguationData":[OSD([subQ5,subQ1,subQ6,subQ7,subQ4,subQ3,subQ2,subQ0])],"isStart":false})})}),makeQuery(id+"F8.opExtrude","SWEPT_FACE",FACE,{"disambiguationData":[OSD([sQuery(id+"F7.wireOp",EDGE,"E67")])]})]});}
            var Q5;
            Q5=makeQuery(id+"F8.boolean.opBoolean","INTERSECT",EDGE,{"disambiguationData":[OD(0.0)],"derivedFrom":[makeQuery(id+"F5.opExtrude","SWEPT_FACE",FACE,{"disambiguationData":[OSD([sQuery(id+"F4.wireOp",EDGE,"E30")])]}),makeQuery(id+"F8.opExtrude","SWEPT_FACE",FACE,{"disambiguationData":[OSD([sQuery(id+"F7.wireOp",EDGE,"E67")])]})]});
            fillet(context, id + "F14", {"entities" : qUnion([Q0, Q1, Q2, Q3, Q4, Q5]), "radius" : 3 * mm, "tangentPropagation" : true, "allowEdgeOverflow" : false});
        }
        {
            var Q0;
            Q0=makeQuery(id+"F1.opExtrude","CAP_EDGE",EDGE,{"disambiguationData":[OSD([sQuery(id+"F0.wireOp",EDGE,"E1.bottom")])],"isStart":false});
            fillet(context, id + "F15", {"entities" : qUnion([Q0]), "radius" : 2 * mm, "tangentPropagation" : true, "allowEdgeOverflow" : false});
        }
        {
            var Q0;
            {var subQ0=sQuery(id+"F0.wireOp",EDGE,"E22.filletArc");var subQ1=sQuery(id+"F0.wireOp",EDGE,"E7");var subQ2=sQuery(id+"F0.wireOp",EDGE,"E6");var subQ3=sQuery(id+"F0.wireOp",EDGE,"E5");var subQ4=sQuery(id+"F0.wireOp",EDGE,"E4");var subQ5=sQuery(id+"F0.wireOp",EDGE,"E1.bottom");var subQ6=sQuery(id+"F0.wireOp",EDGE,"E21.filletArc");var subQ7=sQuery(id+"F0.wireOp",EDGE,"E1.top");var subQ8=sQuery(id+"F0.wireOp",EDGE,"E1.left");var subQ9=sQuery(id+"F0.wireOp",EDGE,"E1.right");var subQ10=sQuery(id+"F0.wireOp",EDGE,"E23.filletArc");var subQ11=sQuery(id+"F0.wireOp",EDGE,"E24.filletArc");Q0=makeQuery(id+"F2.boolean.opBoolean","SPLIT",FACE,{"disambiguationData":[TD([makeQuery(id+"F1.opExtrude","SWEPT_FACE",FACE,{"disambiguationData":[OSD([subQ5])]})])],"derivedFrom":makeQuery(id+"F1.opExtrude","CAP_FACE",FACE,{"disambiguationData":[OSD([subQ5,subQ7,subQ8,subQ9,subQ4,subQ3,subQ2,subQ1,subQ6,subQ0,subQ10,subQ11])],"isStart":true})});}
            var sketch = newSketch(context, id + "F16", { "sketchPlane" : qUnion([Q0])});
            skLineSegment(sketch, "E79.0", {"start": v(-70, 90) * mm, "end": v(70, 90) * mm});
            skArc(sketch, "E80.0", {"start": v(-70, 90) * mm, "mid": v(-77.07, 87.07) * mm, "end": v(-80, 80) * mm});
            skLineSegment(sketch, "E81.0", {"start": v(-80, -80) * mm, "end": v(-80, 80) * mm});
            skArc(sketch, "E82.0", {"start": v(-80, -80) * mm, "mid": v(-77.07, -87.07) * mm, "end": v(-70, -90) * mm});
            skLineSegment(sketch, "E83.0", {"start": v(-70, -90) * mm, "end": v(70, -90) * mm});
            skArc(sketch, "E84.0", {"start": v(70, -90) * mm, "mid": v(77.07, -87.07) * mm, "end": v(80, -80) * mm});
            skLineSegment(sketch, "E85.0", {"start": v(80, -80) * mm, "end": v(80, 80) * mm});
            skArc(sketch, "E86.0", {"start": v(80, 80) * mm, "mid": v(77.07, 87.07) * mm, "end": v(70, 90) * mm});
            skCircle(sketch, "E87.0", {"center": v(-60, 67.5) * mm, "radius": 4 * mm});
            skCircle(sketch, "E88.0", {"center": v(60, 67.5) * mm, "radius": 4 * mm});
            skCircle(sketch, "E89.0", {"center": v(-60, -67.5) * mm, "radius": 4 * mm});
            skCircle(sketch, "E90.0", {"center": v(60, -67.5) * mm, "radius": 4 * mm});
            skArc(sketch, "E91.0", {"start": v(56.15, 48.18) * mm, "mid": v(0, 67.5) * mm, "end": v(-56.15, 48.18) * mm});
            skArc(sketch, "E92.0", {"start": v(-56.15, 48.18) * mm, "mid": v(-58.99, 44.68) * mm, "end": v(-60, 40.3) * mm});
            skLineSegment(sketch, "E93.0", {"start": v(-60, 40.3) * mm, "end": v(-60, -40.3) * mm});
            skArc(sketch, "E94.0", {"start": v(-60, -40.3) * mm, "mid": v(-58.99, -44.68) * mm, "end": v(-56.15, -48.18) * mm});
            skArc(sketch, "E95.0", {"start": v(-56.15, -48.18) * mm, "mid": v(0, -67.5) * mm, "end": v(56.15, -48.18) * mm});
            skArc(sketch, "E96.0", {"start": v(56.15, -48.18) * mm, "mid": v(58.99, -44.68) * mm, "end": v(60, -40.3) * mm});
            skLineSegment(sketch, "E97.0", {"start": v(60, 40.3) * mm, "end": v(60, -40.3) * mm});
            skArc(sketch, "E98.0", {"start": v(60, 40.3) * mm, "mid": v(58.99, 44.68) * mm, "end": v(56.15, 48.18) * mm});
            skLineSegment(sketch, "E99", {"start": v(0, 90) * mm, "end": v(0, 120) * mm, "construction": true});
            skLineSegment(sketch, "E100", {"start": v(-33, 90) * mm, "end": v(-15, 108) * mm});
            skLineSegment(sketch, "E101", {"start": v(-15, 108) * mm, "end": v(-15, 120) * mm});
            skLineSegment(sketch, "E102.MirrorCS", {"start": v(15, 108) * mm, "end": v(15, 120) * mm});
            skLineSegment(sketch, "E103.MirrorCS", {"start": v(33, 90) * mm, "end": v(15, 108) * mm});
            skArc(sketch, "E104", {"start": v(15, 120) * mm, "mid": v(0, 135) * mm, "end": v(-15, 120) * mm});
            skCircle(sketch, "E105", {"center": v(0, 120) * mm, "radius": 6 * mm});
            skLineSegment(sketch, "E106", {"start": v(-80, 0) * mm, "end": v(80, 0) * mm, "construction": true});
            skLineSegment(sketch, "E107.MirrorCS", {"start": v(15, -108) * mm, "end": v(15, -120) * mm});
            skLineSegment(sketch, "E108.MirrorCS", {"start": v(-15, -108) * mm, "end": v(-15, -120) * mm});
            skLineSegment(sketch, "E109.MirrorCS", {"start": v(-33, -90) * mm, "end": v(-15, -108) * mm});
            skArc(sketch, "E110.MirrorCS", {"start": v(15, -120) * mm, "mid": v(0, -135) * mm, "end": v(-15, -120) * mm});
            skLineSegment(sketch, "E111.MirrorCS", {"start": v(0, -90) * mm, "end": v(0, -120) * mm, "construction": true});
            skCircle(sketch, "E112.MirrorC", {"center": v(0, -120) * mm, "radius": 6 * mm});
            skLineSegment(sketch, "E113.MirrorCS", {"start": v(33, -90) * mm, "end": v(15, -108) * mm});
            skSolve(sketch);
        }
        {
            var Q0;
            Q0 = qSketchRegion(id + "F16", true);
            var Q1;
            Q1=makeQuery(id+"F2.opExtrude","CAP_FACE",FACE,{"disambiguationData":[OSD([sQuery(id+"F0.wireOp",EDGE,"E12"),sQuery(id+"F0.wireOp",EDGE,"E13"),sQuery(id+"F0.wireOp",EDGE,"E14"),sQuery(id+"F0.wireOp",EDGE,"E15"),sQuery(id+"F0.wireOp",EDGE,"E17.filletArc"),sQuery(id+"F0.wireOp",EDGE,"E18.filletArc"),sQuery(id+"F0.wireOp",EDGE,"E19.filletArc"),sQuery(id+"F0.wireOp",EDGE,"E20.filletArc"),sQuery(id+"F0.wireOp",EDGE,"E25.0"),sQuery(id+"F0.wireOp",EDGE,"E25.1"),sQuery(id+"F0.wireOp",EDGE,"E25.2"),sQuery(id+"F0.wireOp",EDGE,"E25.3"),sQuery(id+"F0.wireOp",EDGE,"E25.4"),sQuery(id+"F0.wireOp",EDGE,"E25.5"),sQuery(id+"F0.wireOp",EDGE,"E25.6"),sQuery(id+"F0.wireOp",EDGE,"E25.7")])],"isStart":false});
            extrude(context, id + "F17", {"entities" : qUnion([Q0]), "endBound" : BoundingType.UP_TO_SURFACE, "endBoundEntityFace" : qUnion([Q1]), "depth" : 25 * mm});
        }
        {
            var Q0;
            Q0=makeQuery(id+"F17.opExtrude","CAP_EDGE",EDGE,{"disambiguationData":[OSD([sQuery(id+"F16.wireOp",EDGE,"E81.0")])],"isStart":false});
            fillet(context, id + "F18", {"entities" : qUnion([Q0]), "radius" : 2 * mm, "tangentPropagation" : true, "allowEdgeOverflow" : false});
        }
    });
